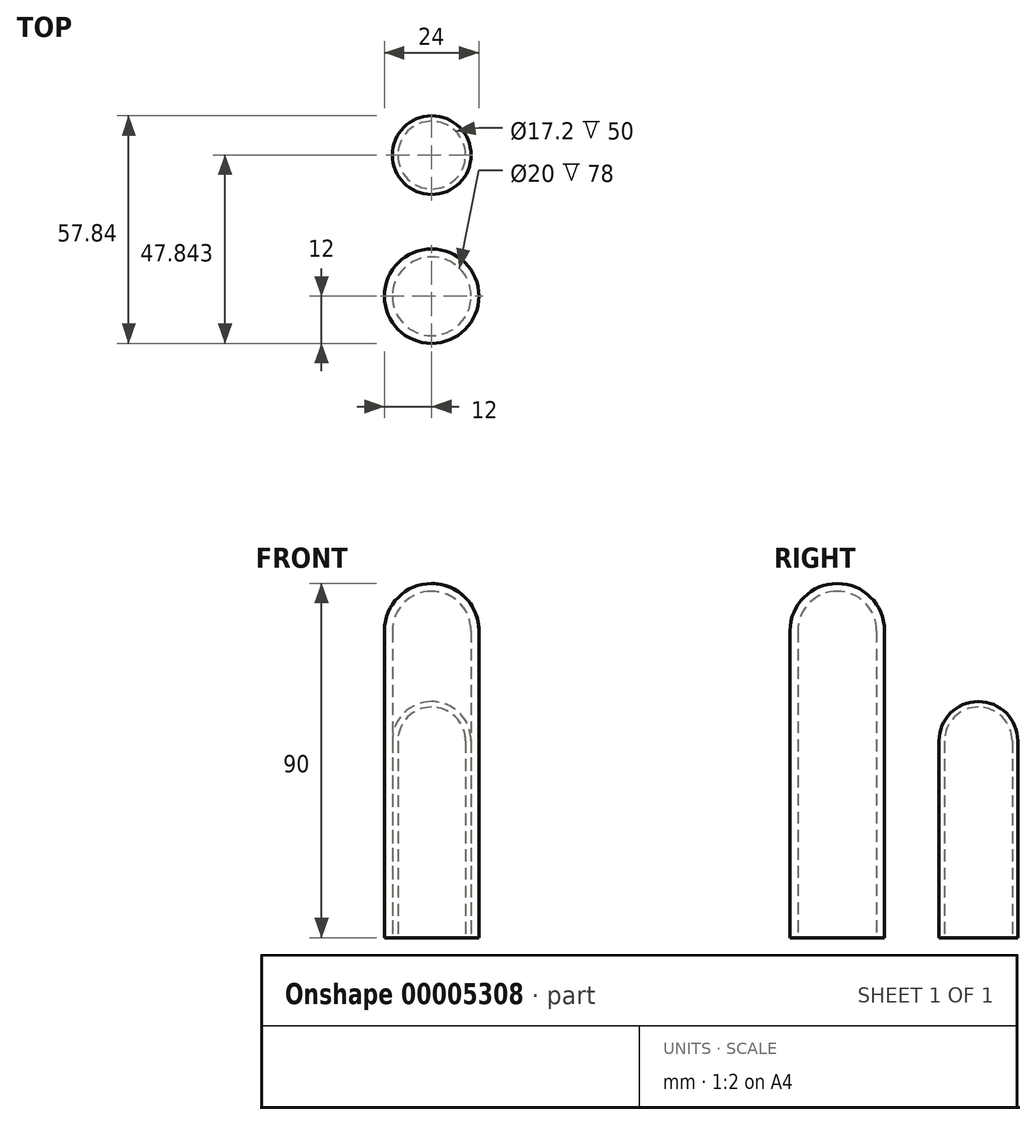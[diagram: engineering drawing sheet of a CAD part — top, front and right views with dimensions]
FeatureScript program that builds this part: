
annotation { "Feature Type Name" : "Feature", "Feature Type Description" : "" }
export const myFeature = defineFeature(function(context is Context, id is Id, definition is map)
    precondition{}
    {
        {
            var Q0;
            Q0=qCreatedBy(makeId("Top.planeOp"),FACE);
            var sketch = newSketch(context, id + "F0", { "sketchPlane" : qUnion([Q0])});
            skCircle(sketch, "E0", {"center": v(0, 0) * mm, "radius": 12 * mm});
            skCircle(sketch, "E1", {"center": v(0, 35.84) * mm, "radius": 10 * mm});
            skSolve(sketch);
        }
        {
            var Q0;
            Q0=makeQuery(id+"F0.imprint","IMPRINT",FACE,{"disambiguationData":[TD([[makeQuery(id+"F0.imprint","IMPRINT",EDGE,{"derivedFrom":sQuery(id+"F0.wireOp",EDGE,"E0")}),1.0]])]});
            extrude(context, id + "F1", {"entities" : qUnion([Q0]), "depth" : 90 * mm});
        }
        {
            var Q0;
            Q0=makeQuery(id+"F1.opExtrude","CAP_FACE",FACE,{"disambiguationData":[OSD([sQuery(id+"F0.wireOp",EDGE,"E0")])],"isStart":false});
            fillet(context, id + "F2", {"entities" : qUnion([Q0]), "radius" : 12 * mm, "tangentPropagation" : true, "allowEdgeOverflow" : false});
        }
        {
            var Q0;
            Q0=makeQuery(id+"F1.opExtrude","CAP_FACE",FACE,{"disambiguationData":[OSD([sQuery(id+"F0.wireOp",EDGE,"E0")])],"isStart":true});
            shell(context, id + "F3", {"entities" : qUnion([Q0]), "thickness" : 2 * mm});
        }
        {
            var Q0;
            Q0=makeQuery(id+"F0.imprint","IMPRINT",FACE,{"disambiguationData":[TD([[makeQuery(id+"F0.imprint","IMPRINT",EDGE,{"derivedFrom":sQuery(id+"F0.wireOp",EDGE,"E1")}),1.0]])]});
            extrude(context, id + "F4", {"entities" : qUnion([Q0]), "depth" : 60 * mm});
        }
        {
            var Q0;
            Q0=makeQuery(id+"F4.opExtrude","CAP_EDGE",EDGE,{"disambiguationData":[OSD([sQuery(id+"F0.wireOp",EDGE,"E1")])],"isStart":false});
            fillet(context, id + "F5", {"entities" : qUnion([Q0]), "radius" : 10 * mm, "tangentPropagation" : true, "allowEdgeOverflow" : false});
        }
        {
            var Q0;
            Q0=makeQuery(id+"F4.opExtrude","CAP_FACE",FACE,{"disambiguationData":[OSD([sQuery(id+"F0.wireOp",EDGE,"E1")])],"isStart":true});
            shell(context, id + "F6", {"entities" : qUnion([Q0]), "thickness" : 1.4 * mm});
        }
    });
